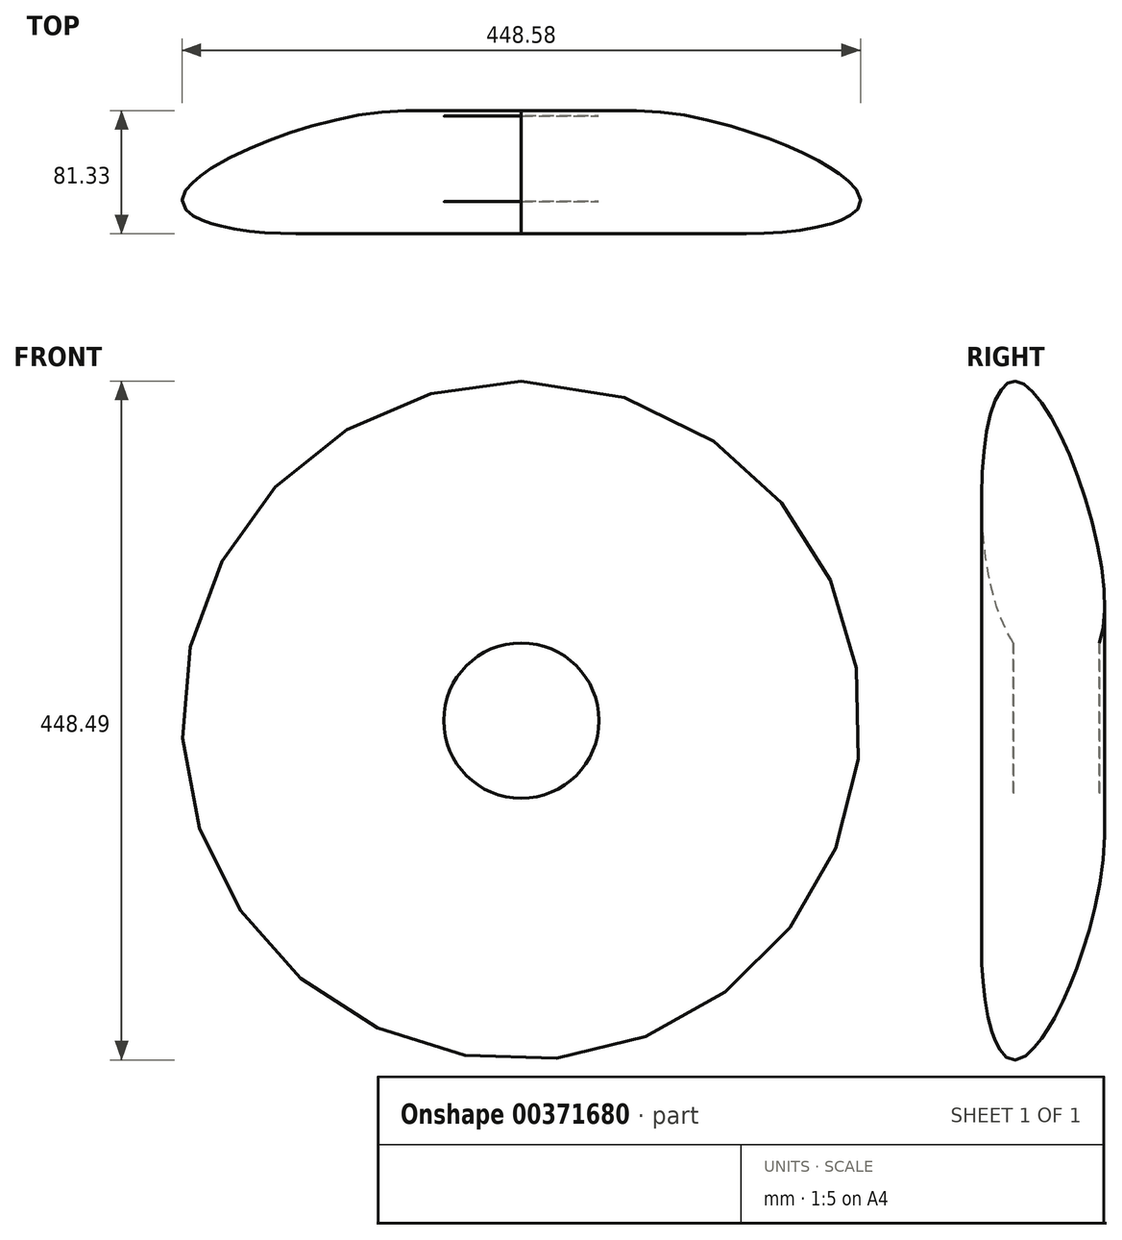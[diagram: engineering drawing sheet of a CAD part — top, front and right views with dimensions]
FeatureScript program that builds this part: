
annotation { "Feature Type Name" : "Feature", "Feature Type Description" : "" }
export const myFeature = defineFeature(function(context is Context, id is Id, definition is map)
    precondition{}
    {
        {
            var Q0;
            Q0=qCreatedBy(makeId("Right.planeOp"),FACE);
            var sketch = newSketch(context, id + "F0", { "sketchPlane" : qUnion([Q0])});
            skLineSegment(sketch, "E0", {"start": v(0, 0) * mm, "end": v(0, -51.32) * mm});
            skLineSegment(sketch, "E1", {"start": v(0, -51.32) * mm, "end": v(-56.58, -51.32) * mm});
            skLineSegment(sketch, "E2", {"start": v(-56.58, -51.32) * mm, "end": v(-56.58, 0) * mm});
            skFitSpline(sketch, "E3", {"points": [v(0, 0) * mm, v(-56.58, 0) * mm, v(-56.58, 172.95) * mm, v(0, 0) * mm]});
            skSolve(sketch);
        }
        {
            var Q0;
            {var subQ0=sQuery(id+"F0.wireOp",EDGE,"E3");var subQ1=makeQuery(id+"F0.imprint","INTERSECT",VERTEX,{"derivedFrom":[sQuery(id+"F0.wireOp",EDGE,"E0"),subQ0]});Q0=makeQuery(id+"F0.imprint","IMPRINT",FACE,{"disambiguationData":[TD([[makeQuery(id+"F0.imprint","IMPRINT",EDGE,{"disambiguationData":[TD([[subQ1,-1.0]])],"derivedFrom":subQ0}),-1.0]])]});}
            var Q1;
            {var subQ0=sQuery(id+"F0.wireOp",EDGE,"E0");Q1=makeQuery(id+"F0.imprint","IMPRINT",FACE,{"disambiguationData":[TD([[makeQuery(id+"F0.imprint","IMPRINT",EDGE,{"derivedFrom":subQ0}),-1.0]])]});}
            var Q2;
            Q2=sQuery(id+"F0.wireOp",EDGE,"E1");
            revolve(context, id + "F1", {"entities" : qUnion([Q0, Q1]), "axis" : qUnion([Q2]), "revolveType" : RevolveType.FULL});
        }
    });
